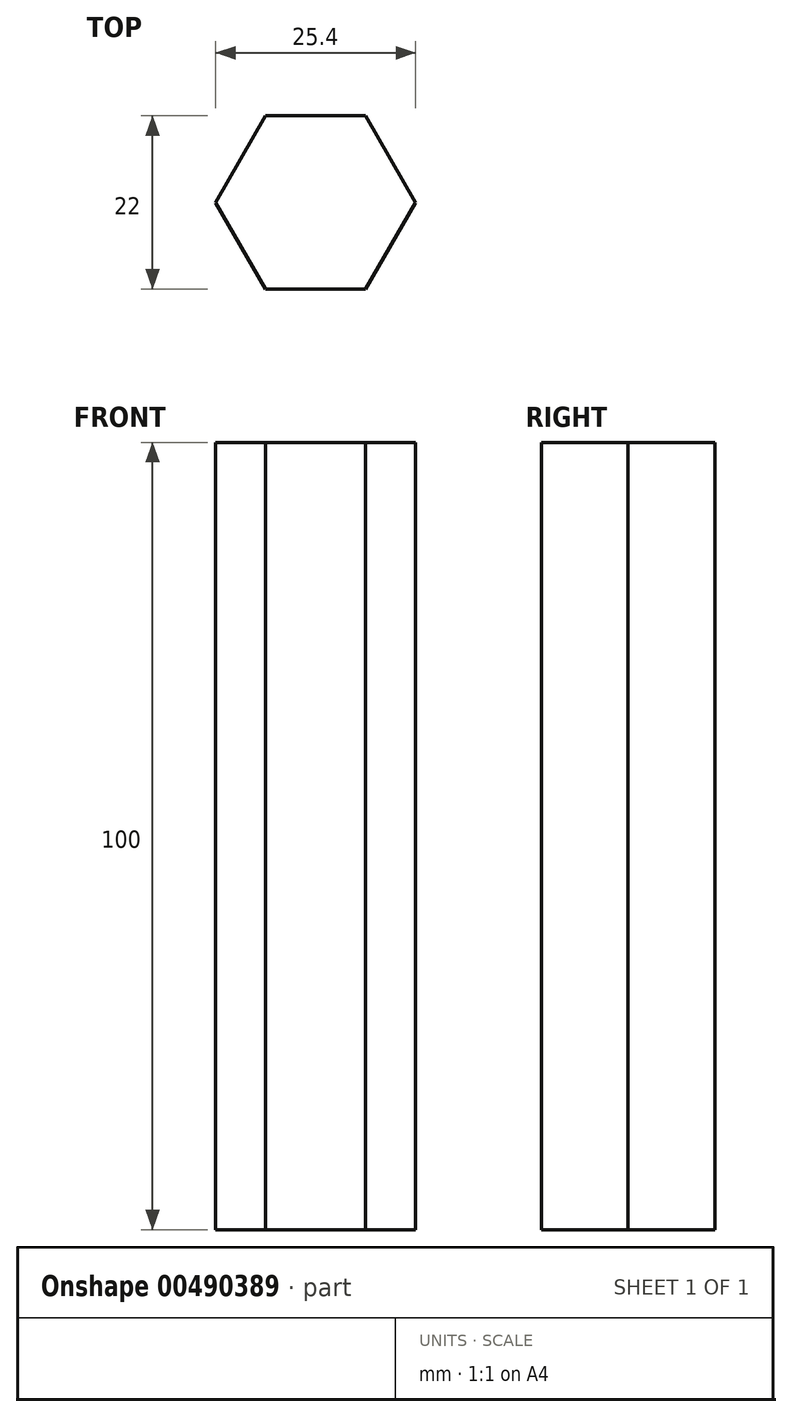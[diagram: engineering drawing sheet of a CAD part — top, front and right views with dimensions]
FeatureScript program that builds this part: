
annotation { "Feature Type Name" : "Feature", "Feature Type Description" : "" }
export const myFeature = defineFeature(function(context is Context, id is Id, definition is map)
    precondition{}
    {
        {
            var Q0;
            Q0=qCreatedBy(makeId("Top.planeOp"),FACE);
            var sketch = newSketch(context, id + "F0", { "sketchPlane" : qUnion([Q0])});
            skCircle(sketch, "E0.cCircle", {"center": v(0, 0) * mm, "radius": 11 * mm, "construction": true});
            skLineSegment(sketch, "E0.0", {"start": v(12.7, 0) * mm, "end": v(6.35, -11) * mm});
            skLineSegment(sketch, "E0.1", {"start": v(6.35, -11) * mm, "end": v(-6.35, -11) * mm});
            skLineSegment(sketch, "E0.2", {"start": v(-6.35, -11) * mm, "end": v(-12.7, 0) * mm});
            skLineSegment(sketch, "E0.3", {"start": v(-12.7, 0) * mm, "end": v(-6.35, 11) * mm});
            skLineSegment(sketch, "E0.4", {"start": v(-6.35, 11) * mm, "end": v(6.35, 11) * mm});
            skLineSegment(sketch, "E0.5", {"start": v(6.35, 11) * mm, "end": v(12.7, 0) * mm});
            skPoint(sketch, "E0.0.midPoint", {"position": v(9.53, -5.5) * mm});
            skSolve(sketch);
        }
        {
            var Q0;
            Q0 = qSketchRegion(id + "F0", true);
            extrude(context, id + "F1", {"entities" : qUnion([Q0]), "depth" : 100 * mm});
        }
    });
